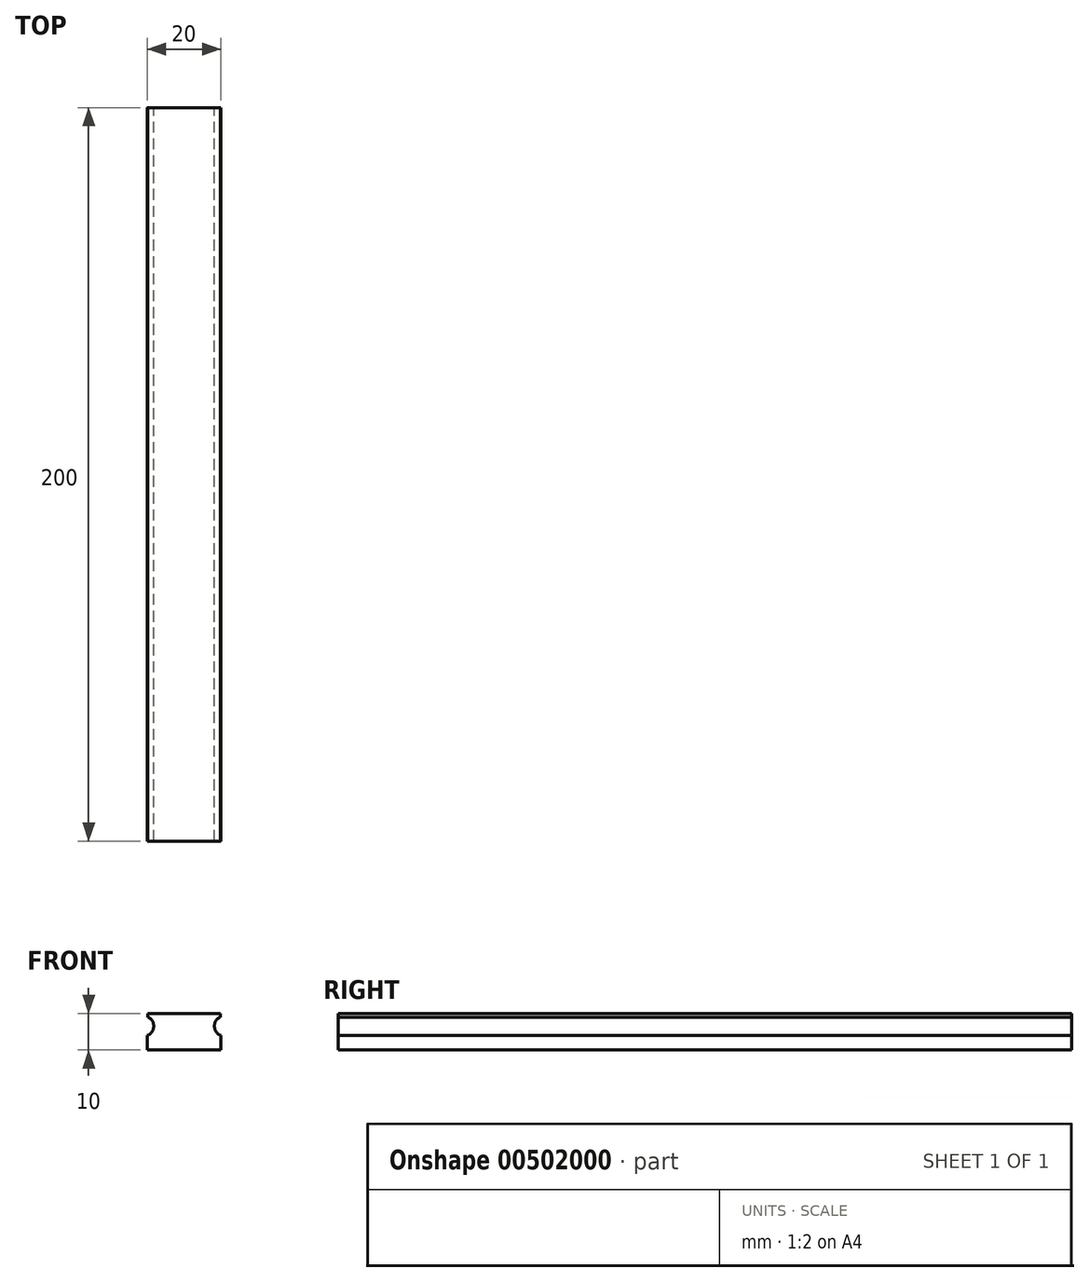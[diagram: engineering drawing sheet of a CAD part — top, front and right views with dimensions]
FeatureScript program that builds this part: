
annotation { "Feature Type Name" : "Feature", "Feature Type Description" : "" }
export const myFeature = defineFeature(function(context is Context, id is Id, definition is map)
    precondition{}
    {
        {
            var Q0;
            Q0=qCreatedBy(makeId("Front.planeOp"),FACE);
            var sketch = newSketch(context, id + "F0", { "sketchPlane" : qUnion([Q0])});
            skLineSegment(sketch, "E0", {"start": v(0, 0) * mm, "end": v(10, 0) * mm});
            skLineSegment(sketch, "E1", {"start": v(10, 0) * mm, "end": v(10, 4) * mm});
            skLineSegment(sketch, "E2", {"start": v(9.87, 10) * mm, "end": v(0, 10) * mm});
            skLineSegment(sketch, "E3", {"start": v(0, 0) * mm, "end": v(0, 10) * mm, "construction": true});
            skLineSegment(sketch, "E4.MirrorCS", {"start": v(-9.87, 10) * mm, "end": v(0, 10) * mm});
            skLineSegment(sketch, "E5.MirrorCS", {"start": v(-10, 0) * mm, "end": v(-10, 4) * mm});
            skLineSegment(sketch, "E6.MirrorCS", {"start": v(0, 0) * mm, "end": v(-10, 0) * mm});
            skPoint(sketch, "E7", {"position": v(0, 5) * mm});
            skLineSegment(sketch, "E8", {"start": v(9.87, 10) * mm, "end": v(9.87, 9) * mm});
            skArc(sketch, "E9", {"start": v(9.87, 9) * mm, "mid": v(8.28, 6.46) * mm, "end": v(10, 4) * mm});
            skArc(sketch, "E10.MirrorCS", {"start": v(-9.87, 9) * mm, "mid": v(-8.28, 6.46) * mm, "end": v(-10, 4) * mm});
            skLineSegment(sketch, "E11.MirrorCS", {"start": v(-9.87, 10) * mm, "end": v(-9.87, 9) * mm});
            skSolve(sketch);
        }
        {
            assignVariable(context, id + "F1", {"name" : "length", "anyValue" : 200 * mm});
        }
        {
            var Q0;
            Q0=makeQuery(id+"F0.imprint","IMPRINT",FACE,{"disambiguationData":[TD([[makeQuery(id+"F0.imprint","IMPRINT",EDGE,{"derivedFrom":sQuery(id+"F0.wireOp",EDGE,"E0")}),1.0]])]});
            extrude(context, id + "F2", {"entities" : qUnion([Q0]), "depth" : getVariable(context, 'length')});
        }
    });
